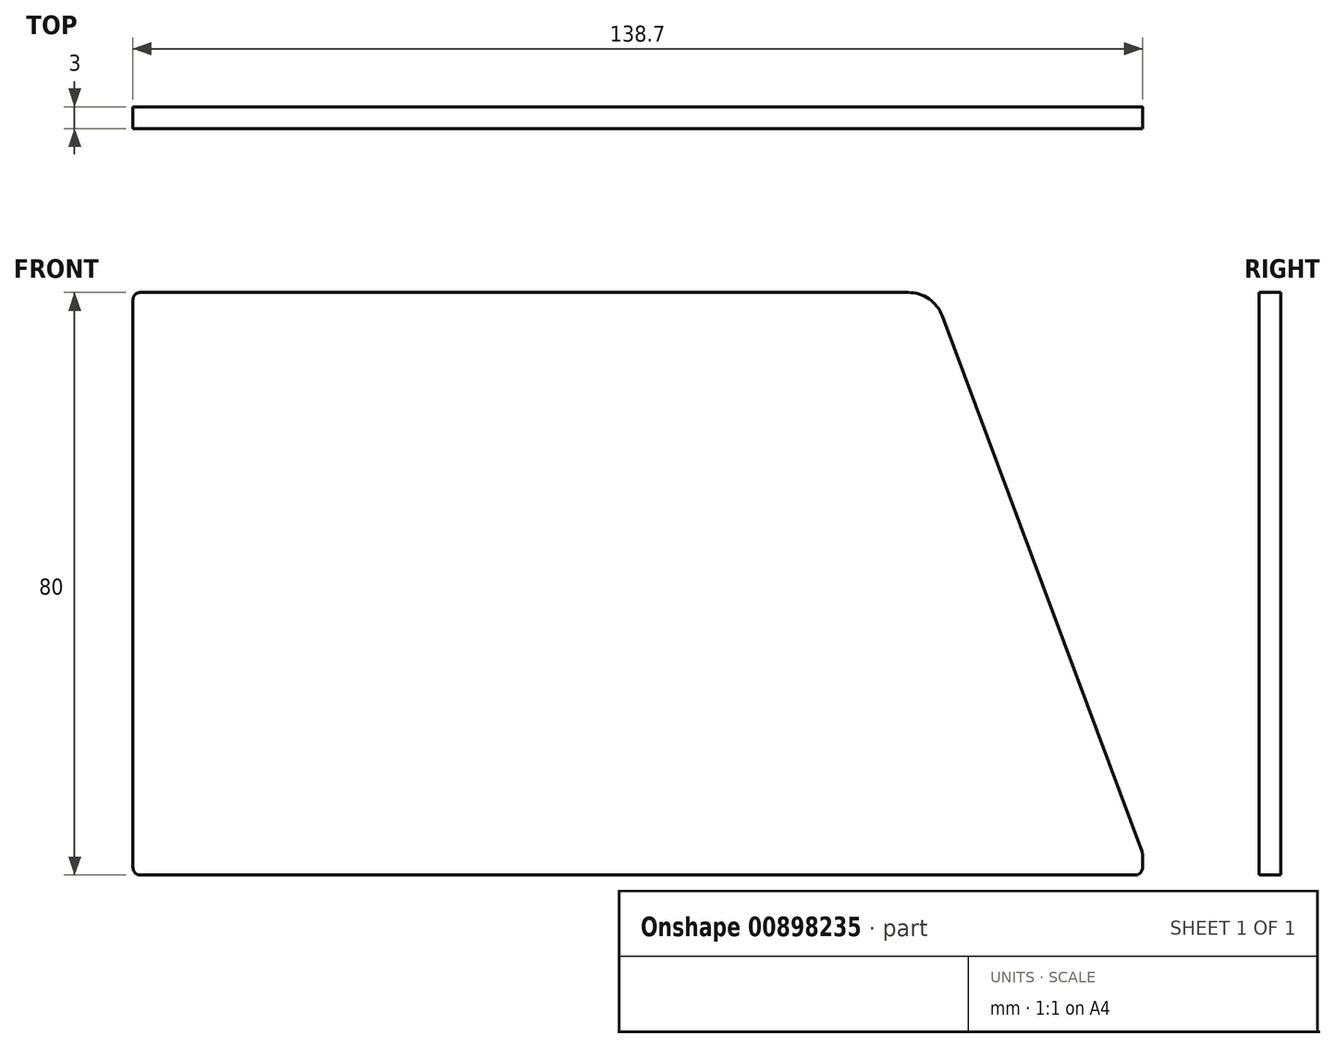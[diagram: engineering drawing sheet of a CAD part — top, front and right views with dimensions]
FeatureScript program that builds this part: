
annotation { "Feature Type Name" : "Feature", "Feature Type Description" : "" }
export const myFeature = defineFeature(function(context is Context, id is Id, definition is map)
    precondition{}
    {
        {
            var Q0;
            Q0=qCreatedBy(makeId("Front.planeOp"),FACE);
            var sketch = newSketch(context, id + "F0", { "sketchPlane" : qUnion([Q0])});
            skLineSegment(sketch, "E0.bottom", {"start": v(0, 0) * mm, "end": v(138.7, 0) * mm});
            skLineSegment(sketch, "E0.top", {"start": v(0, 80) * mm, "end": v(106.53, 80) * mm});
            skLineSegment(sketch, "E0.left", {"start": v(0, 0) * mm, "end": v(0, 80) * mm});
            skLineSegment(sketch, "E0.right", {"start": v(138.7, 0) * mm, "end": v(138.7, 3) * mm});
            skPoint(sketch, "E1.visualSharp", {"position": v(138.7, 80) * mm});
            skLineSegment(sketch, "E2", {"start": v(138.7, 3) * mm, "end": v(111.21, 76.75) * mm});
            skPoint(sketch, "E3.visualSharp", {"position": v(110, 80) * mm});
            skArc(sketch, "E3.filletArc", {"start": v(111.21, 76.75) * mm, "mid": v(109.38, 79.1) * mm, "end": v(106.53, 80) * mm});
            skSolve(sketch);
        }
        {
            var Q0;
            Q0=qSketchRegion(id+"F0",true);
            extrude(context, id + "F1", {"entities" : qUnion([Q0]), "endBound" : BoundingType.SYMMETRIC, "depth" : 3 * mm});
        }
        {
            var Q0;
            Q0=makeQuery(id+"F1.opExtrude","SWEPT_EDGE",EDGE,{"disambiguationData":[OSD([sQuery(id+"F0.wireOp",EDGE,"E0.bottom"),sQuery(id+"F0.wireOp",EDGE,"E0.right")])]});
            var Q1;
            Q1=makeQuery(id+"F1.opExtrude","SWEPT_EDGE",EDGE,{"disambiguationData":[OSD([sQuery(id+"F0.wireOp",EDGE,"E0.right"),sQuery(id+"F0.wireOp",EDGE,"E2")])]});
            var Q2;
            Q2=makeQuery(id+"F1.opExtrude","SWEPT_EDGE",EDGE,{"disambiguationData":[OSD([sQuery(id+"F0.wireOp",EDGE,"E0.top"),sQuery(id+"F0.wireOp",EDGE,"E0.left")])]});
            var Q3;
            Q3=makeQuery(id+"F1.opExtrude","SWEPT_EDGE",EDGE,{"disambiguationData":[OSD([sQuery(id+"F0.wireOp",EDGE,"E0.bottom"),sQuery(id+"F0.wireOp",EDGE,"E0.left")])]});
            fillet(context, id + "F2", {"entities" : qUnion([Q0, Q1, Q2, Q3]), "radius" : 1 * mm, "tangentPropagation" : true, "allowEdgeOverflow" : false});
        }
    });
